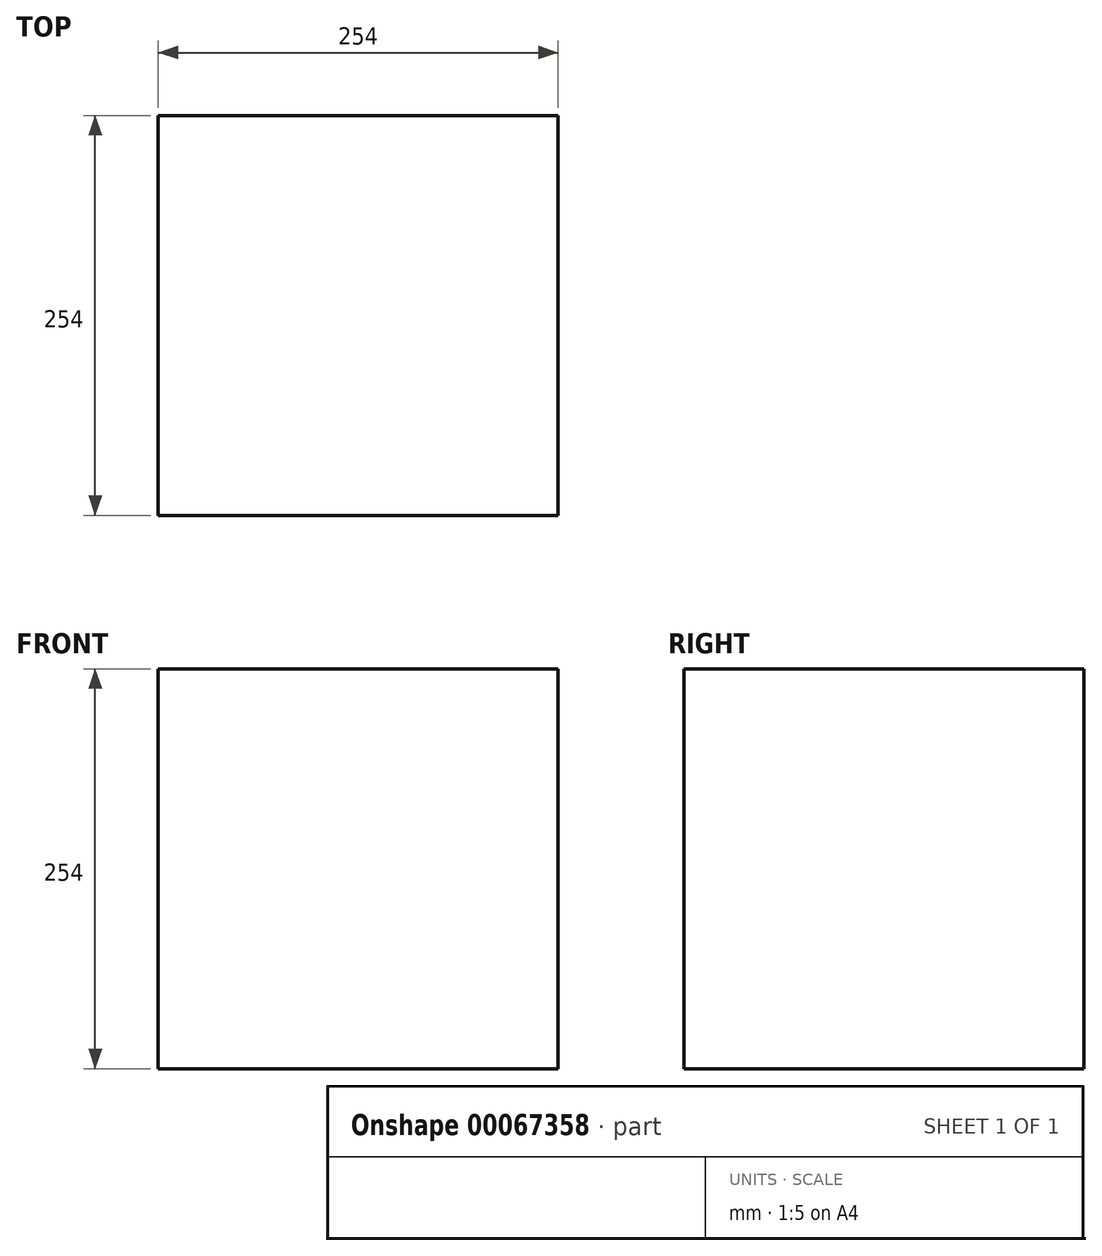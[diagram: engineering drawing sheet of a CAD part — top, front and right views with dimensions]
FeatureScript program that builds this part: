
annotation { "Feature Type Name" : "Feature", "Feature Type Description" : "" }
export const myFeature = defineFeature(function(context is Context, id is Id, definition is map)
    precondition{}
    {
        {
            var Q0;
            Q0=qCreatedBy(makeId("Front.planeOp"),FACE);
            var sketch = newSketch(context, id + "F0", { "sketchPlane" : qUnion([Q0])});
            skLineSegment(sketch, "E0.rect.bottom", {"start": v(-127, 127) * mm, "end": v(127, 127) * mm});
            skLineSegment(sketch, "E0.rect.top", {"start": v(-127, -127) * mm, "end": v(127, -127) * mm});
            skLineSegment(sketch, "E0.rect.left", {"start": v(-127, 127) * mm, "end": v(-127, -127) * mm});
            skLineSegment(sketch, "E0.rect.right", {"start": v(127, 127) * mm, "end": v(127, -127) * mm});
            skPoint(sketch, "E0.rect.middle", {"position": v(0, 0) * mm});
            skSolve(sketch);
        }
        {
            var Q0;
            Q0=makeQuery(id+"F0.imprint","IMPRINT",FACE,{"disambiguationData":[TD([[makeQuery(id+"F0.imprint","IMPRINT",EDGE,{"derivedFrom":sQuery(id+"F0.wireOp",EDGE,"E0.rect.bottom")}),-1.0]])]});
            extrude(context, id + "F1", {"entities" : qUnion([Q0]), "depth" : 127 * mm, "hasSecondDirection" : true, "secondDirectionOppositeDirection" : true, "secondDirectionDepth" : 127 * mm});
        }
    });
